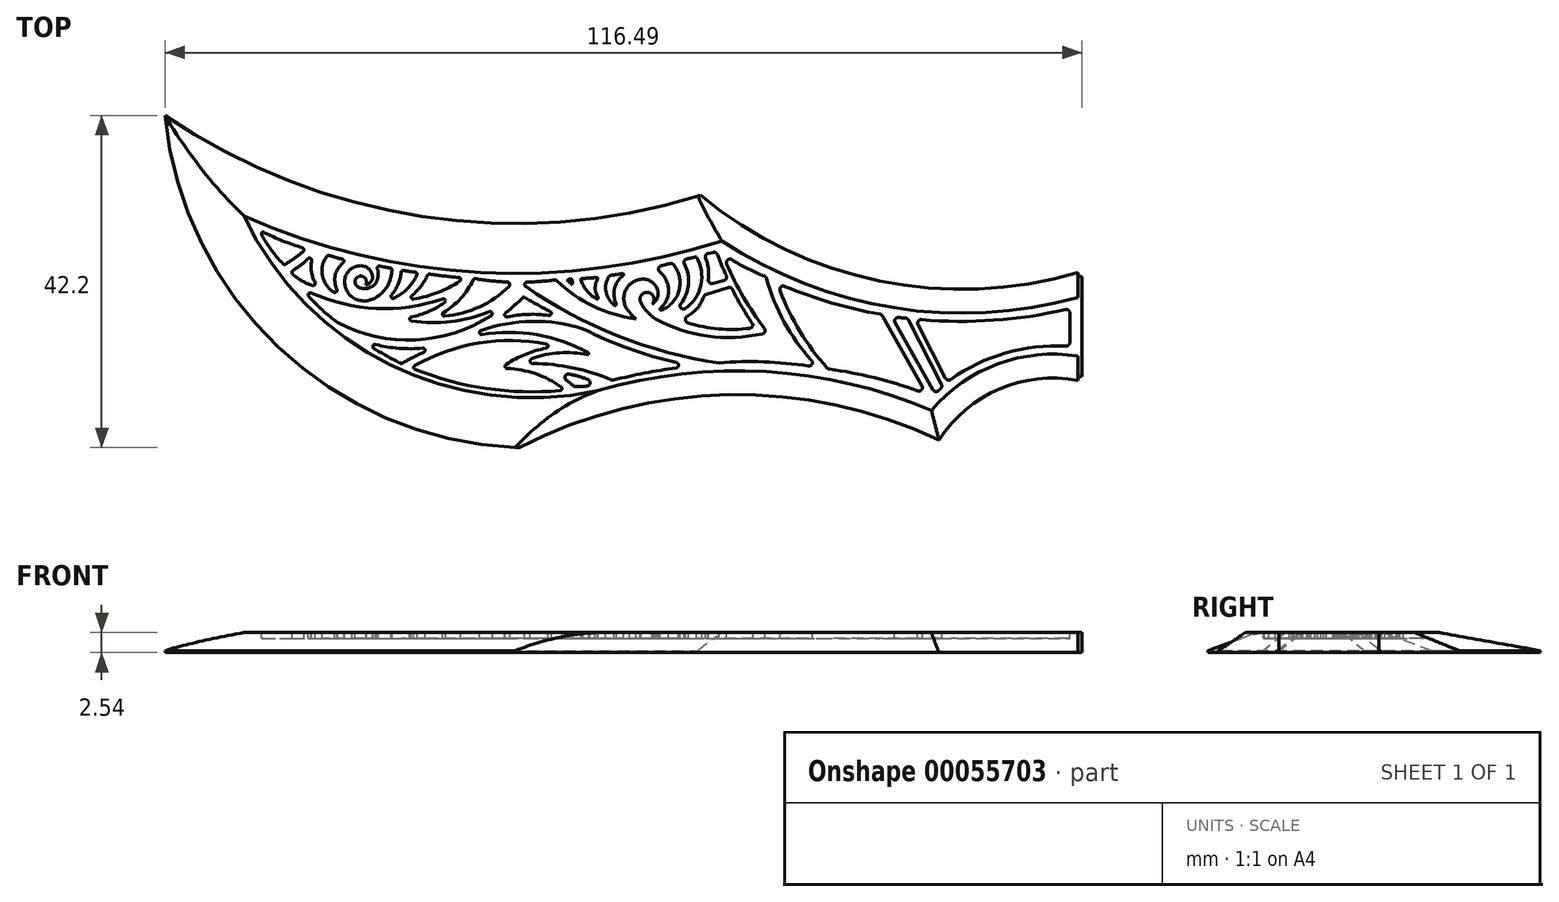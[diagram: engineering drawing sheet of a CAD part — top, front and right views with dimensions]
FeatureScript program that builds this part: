
annotation { "Feature Type Name" : "Feature", "Feature Type Description" : "" }
export const myFeature = defineFeature(function(context is Context, id is Id, definition is map)
    precondition{}
    {
        {
            var Q0;
            Q0=qCreatedBy(makeId("Top.planeOp"),FACE);
            var sketch = newSketch(context, id + "F0", { "sketchPlane" : qUnion([Q0])});
            skLineSegment(sketch, "E0", {"start": v(52.01, 15.28) * mm, "end": v(52.01, 0) * mm});
            skArc(sketch, "E1", {"start": v(4.94, 24.58) * mm, "mid": v(27.32, 14.1) * mm, "end": v(52.01, 15.28) * mm});
            skArc(sketch, "E2", {"start": v(-63.97, 34.45) * mm, "mid": v(-30.66, 21.52) * mm, "end": v(4.94, 24.58) * mm});
            skArc(sketch, "E3", {"start": v(-63.97, 34.45) * mm, "mid": v(-48.77, 4.29) * mm, "end": v(-17.2, -7.77) * mm});
            skArc(sketch, "E4", {"start": v(34.67, -7.77) * mm, "mid": v(8.73, -1.81) * mm, "end": v(-17.2, -7.77) * mm});
            skArc(sketch, "E5", {"start": v(52.01, 0) * mm, "mid": v(42.1, -1.13) * mm, "end": v(34.67, -7.77) * mm});
            skLineSegment(sketch, "E6.bottom", {"start": v(52.01, 15.28) * mm, "end": v(52.52, 15.28) * mm});
            skLineSegment(sketch, "E6.top", {"start": v(52.01, 0) * mm, "end": v(52.52, 0) * mm});
            skLineSegment(sketch, "E6.right", {"start": v(52.52, 15.28) * mm, "end": v(52.52, 0) * mm});
            skLineSegment(sketch, "E7", {"start": v(52.01, 13.97) * mm, "end": v(52.52, 13.97) * mm});
            skLineSegment(sketch, "E8", {"start": v(52.01, 1.27) * mm, "end": v(52.52, 1.27) * mm});
            skSolve(sketch);
        }
        {
            var Q0;
            {var subQ4=sQuery(id+"F0.wireOp",EDGE,"E1");Q0=makeQuery(id+"F0.imprint","IMPRINT",FACE,{"disambiguationData":[TD([[makeQuery(id+"F0.imprint","IMPRINT",EDGE,{"derivedFrom":subQ4}),-1.0]])]});}
            extrude(context, id + "F1", {"entities" : qUnion([Q0]), "depth" : 2.54 * mm});
        }
        {
            var Q0;
            Q0=makeQuery(id+"F1.opExtrude","CAP_EDGE",EDGE,{"disambiguationData":[OSD([sQuery(id+"F0.wireOp",EDGE,"E5")])],"isStart":false});
            var Q1;
            Q1=makeQuery(id+"F1.opExtrude","CAP_EDGE",EDGE,{"disambiguationData":[OSD([sQuery(id+"F0.wireOp",EDGE,"E1")])],"isStart":false});
            var Q2;
            Q2=makeQuery(id+"F1.opExtrude","CAP_EDGE",EDGE,{"disambiguationData":[OSD([sQuery(id+"F0.wireOp",EDGE,"E4")])],"isStart":false});
            chamfer(context, id + "F2", {"entities" : qUnion([Q0, Q1, Q2]), "chamferType" : ChamferType.OFFSET_ANGLE, "width" : 3.8 * mm, "oppositeDirection" : true, "angle" : 40 * degree, "tangentPropagation" : true});
        }
        {
            var Q0;
            Q0=makeQuery(id+"F1.opExtrude","CAP_EDGE",EDGE,{"disambiguationData":[OSD([sQuery(id+"F0.wireOp",EDGE,"E2")])],"isStart":false});
            var Q1;
            Q1=makeQuery(id+"F1.opExtrude","CAP_EDGE",EDGE,{"disambiguationData":[OSD([sQuery(id+"F0.wireOp",EDGE,"E3")])],"isStart":false});
            chamfer(context, id + "F3", {"entities" : qUnion([Q0, Q1]), "chamferType" : ChamferType.OFFSET_ANGLE, "width" : 6.35 * mm, "oppositeDirection" : true, "angle" : 20 * degree, "tangentPropagation" : true});
        }
        {
            var Q0;
            Q0=makeQuery(id+"F1.opExtrude","CAP_FACE",FACE,{"disambiguationData":[OSD([sQuery(id+"F0.wireOp",EDGE,"E1"),sQuery(id+"F0.wireOp",EDGE,"E2"),sQuery(id+"F0.wireOp",EDGE,"E3"),sQuery(id+"F0.wireOp",EDGE,"E4"),sQuery(id+"F0.wireOp",EDGE,"E5"),sQuery(id+"F0.wireOp",EDGE,"E0")])],"isStart":false});
            var sketch = newSketch(context, id + "F4", { "sketchPlane" : qUnion([Q0])});
            skPoint(sketch, "E9", {"position": v(-53.92, 21.64) * mm});
            skPoint(sketch, "E10", {"position": v(6.79, 18.5) * mm});
            skPoint(sketch, "E11", {"position": v(52.01, 11.32) * mm});
            skPoint(sketch, "E12", {"position": v(52.01, 3.87) * mm});
            skPoint(sketch, "E13", {"position": v(33.4, -3.01) * mm});
            skPoint(sketch, "E14", {"position": v(-8.98, -0.53) * mm});
            skArc(sketch, "E15", {"start": v(-53.92, 21.64) * mm, "mid": v(-23.86, 14.49) * mm, "end": v(6.79, 18.5) * mm});
            skArc(sketch, "E16", {"start": v(6.79, 18.5) * mm, "mid": v(28.62, 10) * mm, "end": v(52.01, 11.32) * mm});
            skArc(sketch, "E17", {"start": v(-53.92, 21.64) * mm, "mid": v(-35.3, 2.75) * mm, "end": v(-8.98, -0.53) * mm});
            skArc(sketch, "E18", {"start": v(33.4, -3.01) * mm, "mid": v(12.43, 1.9) * mm, "end": v(-8.98, -0.53) * mm});
            skArc(sketch, "E19", {"start": v(52.01, 3.87) * mm, "mid": v(41.8, 2.86) * mm, "end": v(33.4, -3.01) * mm});
            skLineSegment(sketch, "E20", {"start": v(52.01, 11.32) * mm, "end": v(52.01, 3.87) * mm});
            skArc(sketch, "E21", {"start": v(-51.68, 19.31) * mm, "mid": v(-50.46, 17.36) * mm, "end": v(-48.97, 15.6) * mm});
            skArc(sketch, "E22", {"start": v(-51.41, 19.59) * mm, "mid": v(-49, 18.5) * mm, "end": v(-46.5, 17.62) * mm});
            skArc(sketch, "E23", {"start": v(-48.65, 15.55) * mm, "mid": v(-47.5, 16.31) * mm, "end": v(-46.4, 17.16) * mm});
            skPoint(sketch, "E24.visualSharp", {"position": v(-51.95, 19.85) * mm});
            skArc(sketch, "E24.filletArc", {"start": v(-51.41, 19.59) * mm, "mid": v(-51.64, 19.55) * mm, "end": v(-51.68, 19.31) * mm});
            skArc(sketch, "E25", {"start": v(14.75, 12.73) * mm, "mid": v(20.7, 10.64) * mm, "end": v(26.86, 9.2) * mm});
            skArc(sketch, "E26", {"start": v(14.17, 12.17) * mm, "mid": v(16.71, 7) * mm, "end": v(20.16, 2.37) * mm});
            skArc(sketch, "E27", {"start": v(31.66, -0.55) * mm, "mid": v(26.11, 1.13) * mm, "end": v(20.42, 2.23) * mm});
            skArc(sketch, "E28", {"start": v(34.6, -0.23) * mm, "mid": v(34.45, -0.36) * mm, "end": v(34.32, -0.5) * mm});
            skArc(sketch, "E29", {"start": v(8.04, 16.13) * mm, "mid": v(10.07, 14.98) * mm, "end": v(12.2, 14.02) * mm});
            skArc(sketch, "E30", {"start": v(7.4, 15.58) * mm, "mid": v(9.53, 11.34) * mm, "end": v(12.19, 7.4) * mm});
            skArc(sketch, "E31", {"start": v(12.46, 13.73) * mm, "mid": v(14.7, 8.2) * mm, "end": v(18.16, 3.33) * mm});
            skArc(sketch, "E32", {"start": v(-1.66, 8.6) * mm, "mid": v(4.96, 6.42) * mm, "end": v(11.93, 6.7) * mm});
            skArc(sketch, "E33", {"start": v(-2.1, 10.46) * mm, "mid": v(-2.1, 11.7) * mm, "end": v(-3.35, 11.72) * mm});
            skArc(sketch, "E34", {"start": v(-3.35, 11.72) * mm, "mid": v(-3.6, 11.22) * mm, "end": v(-3.5, 10.66) * mm});
            skArc(sketch, "E35", {"start": v(-3.5, 10.66) * mm, "mid": v(-2.73, 9.5) * mm, "end": v(-1.66, 8.6) * mm});
            skArc(sketch, "E36", {"start": v(-2.1, 10.46) * mm, "mid": v(-1.43, 11.25) * mm, "end": v(-1.38, 12.29) * mm});
            skArc(sketch, "E37", {"start": v(-1.38, 12.29) * mm, "mid": v(-2.25, 13.36) * mm, "end": v(-3.6, 13.6) * mm});
            skArc(sketch, "E38", {"start": v(-3.6, 13.6) * mm, "mid": v(-5.56, 11.94) * mm, "end": v(-4.95, 9.45) * mm});
            skArc(sketch, "E39", {"start": v(-17.93, 13.29) * mm, "mid": v(-16.2, 13.36) * mm, "end": v(-14.47, 13.54) * mm});
            skArc(sketch, "E40", {"start": v(-18.12, 12.68) * mm, "mid": v(-6.4, 6.42) * mm, "end": v(6.42, 3.01) * mm});
            skArc(sketch, "E41", {"start": v(17.77, 2.6) * mm, "mid": v(12.1, 3.14) * mm, "end": v(6.42, 3.01) * mm});
            skArc(sketch, "E42", {"start": v(-4.95, 9.45) * mm, "mid": v(-4.58, 9) * mm, "end": v(-4.15, 8.6) * mm});
            skArc(sketch, "E43", {"start": v(-14.19, 13.45) * mm, "mid": v(-9.56, 10.2) * mm, "end": v(-4.15, 8.6) * mm});
            skArc(sketch, "E44", {"start": v(-10.83, 7.33) * mm, "mid": v(-5.03, 4.82) * mm, "end": v(1.02, 3.03) * mm});
            skArc(sketch, "E45", {"start": v(-10.83, 7.33) * mm, "mid": v(-17.34, 8.28) * mm, "end": v(-23.83, 7.13) * mm});
            skArc(sketch, "E46", {"start": v(-10.21, 4.3) * mm, "mid": v(-16.76, 6.59) * mm, "end": v(-23.7, 6.62) * mm});
            skArc(sketch, "E47", {"start": v(-10.3, 4.04) * mm, "mid": v(-13.86, 4.28) * mm, "end": v(-17.34, 3.56) * mm});
            skArc(sketch, "E48", {"start": v(-7.22, 0.83) * mm, "mid": v(-12.12, 2.38) * mm, "end": v(-17.23, 2.91) * mm});
            skArc(sketch, "E49", {"start": v(1, 2.37) * mm, "mid": v(-3.03, 1.7) * mm, "end": v(-7, 0.82) * mm});
            skArc(sketch, "E50", {"start": v(-42.02, 8.13) * mm, "mid": v(-32.13, 5.91) * mm, "end": v(-22.5, 9.04) * mm});
            skArc(sketch, "E51", {"start": v(-32.63, 8.34) * mm, "mid": v(-27.6, 8.25) * mm, "end": v(-22.74, 9.5) * mm});
            skArc(sketch, "E52", {"start": v(-32.64, 8.86) * mm, "mid": v(-30.45, 9.53) * mm, "end": v(-28.45, 10.65) * mm});
            skArc(sketch, "E53", {"start": v(-45.4, 11.89) * mm, "mid": v(-37.12, 9.93) * mm, "end": v(-28.7, 11.12) * mm});
            skArc(sketch, "E54", {"start": v(-45.7, 11.47) * mm, "mid": v(-43.95, 9.7) * mm, "end": v(-42.02, 8.13) * mm});
            skArc(sketch, "E55", {"start": v(-1.03, 9.95) * mm, "mid": v(0.02, 12.27) * mm, "end": v(-1.1, 14.56) * mm});
            skPoint(sketch, "E55.startSnap0", {"position": v(-30.5, 9.5) * mm});
            skArc(sketch, "E56", {"start": v(-0.93, 15.34) * mm, "mid": v(-0.37, 15.48) * mm, "end": v(0.18, 15.63) * mm});
            skArc(sketch, "E57", {"start": v(-0.9, 9.72) * mm, "mid": v(1.35, 12.2) * mm, "end": v(0.65, 15.48) * mm});
            skArc(sketch, "E58", {"start": v(1.57, 10.55) * mm, "mid": v(2.54, 12.99) * mm, "end": v(2.01, 15.56) * mm});
            skArc(sketch, "E59", {"start": v(2.17, 9.92) * mm, "mid": v(4.14, 12.93) * mm, "end": v(3.53, 16.48) * mm});
            skArc(sketch, "E60", {"start": v(2.3, 16.2) * mm, "mid": v(2.92, 16.34) * mm, "end": v(3.53, 16.48) * mm});
            skArc(sketch, "E61", {"start": v(-7.41, 14.12) * mm, "mid": v(-6.63, 14.23) * mm, "end": v(-5.84, 14.35) * mm});
            skArc(sketch, "E62", {"start": v(-5.74, 14.1) * mm, "mid": v(-6.84, 12.46) * mm, "end": v(-6.64, 10.49) * mm});
            skArc(sketch, "E63", {"start": v(-7.5, 14.06) * mm, "mid": v(-7.94, 12.05) * mm, "end": v(-6.85, 10.32) * mm});
            skArc(sketch, "E64", {"start": v(-11, 13.73) * mm, "mid": v(-10.07, 13.78) * mm, "end": v(-9.13, 13.85) * mm});
            skArc(sketch, "E65", {"start": v(-9, 13.65) * mm, "mid": v(-9.3, 12.47) * mm, "end": v(-8.94, 11.32) * mm});
            skArc(sketch, "E66", {"start": v(-11.13, 13.55) * mm, "mid": v(-10.35, 12.16) * mm, "end": v(-9.12, 11.13) * mm});
            skArc(sketch, "E67", {"start": v(-12.67, 13.62) * mm, "mid": v(-12.53, 13.63) * mm, "end": v(-12.4, 13.65) * mm});
            skArc(sketch, "E68", {"start": v(-12.75, 13.39) * mm, "mid": v(-12.57, 13.22) * mm, "end": v(-12.37, 13.07) * mm});
            skArc(sketch, "E69", {"start": v(-12.25, 13.54) * mm, "mid": v(-12.21, 13.38) * mm, "end": v(-12.16, 13.22) * mm});
            skArc(sketch, "E70", {"start": v(-15.52, 5.4) * mm, "mid": v(-24.12, 5.52) * mm, "end": v(-32.22, 2.66) * mm});
            skArc(sketch, "E71", {"start": v(-15.52, 4.88) * mm, "mid": v(-18.18, 4.1) * mm, "end": v(-20.63, 2.8) * mm});
            skArc(sketch, "E72", {"start": v(-13.64, -0.03) * mm, "mid": v(-16.9, 1.63) * mm, "end": v(-20.5, 2.3) * mm});
            skArc(sketch, "E73", {"start": v(-32.19, 2.18) * mm, "mid": v(-23.14, -0.25) * mm, "end": v(-13.77, -0.52) * mm});
            skArc(sketch, "E74", {"start": v(-31.07, 4.36) * mm, "mid": v(-32.45, 3.7) * mm, "end": v(-33.8, 2.98) * mm});
            skArc(sketch, "E75", {"start": v(-37.22, 5.34) * mm, "mid": v(-34.23, 4.85) * mm, "end": v(-31.2, 4.87) * mm});
            skArc(sketch, "E76", {"start": v(-37.43, 4.86) * mm, "mid": v(-35.76, 3.87) * mm, "end": v(-34.04, 2.97) * mm});
            skArc(sketch, "E77", {"start": v(-37.6, 13.75) * mm, "mid": v(-37.93, 14.8) * mm, "end": v(-38.9, 15.33) * mm});
            skArc(sketch, "E78", {"start": v(-38.9, 15.33) * mm, "mid": v(-40.32, 14.96) * mm, "end": v(-41.1, 13.72) * mm});
            skArc(sketch, "E79", {"start": v(-41.1, 13.72) * mm, "mid": v(-40.97, 12.42) * mm, "end": v(-40.18, 11.37) * mm});
            skArc(sketch, "E80", {"start": v(-40.18, 11.37) * mm, "mid": v(-38.57, 10.88) * mm, "end": v(-36.98, 11.43) * mm});
            skArc(sketch, "E81", {"start": v(-38.43, 13.62) * mm, "mid": v(-39.58, 13.84) * mm, "end": v(-39.45, 12.67) * mm});
            skArc(sketch, "E82", {"start": v(-38.43, 12.89) * mm, "mid": v(-38.37, 13.25) * mm, "end": v(-38.43, 13.62) * mm});
            skArc(sketch, "E83", {"start": v(-38.43, 12.89) * mm, "mid": v(-37.9, 13.2) * mm, "end": v(-37.6, 13.75) * mm});
            skArc(sketch, "E84", {"start": v(-39.45, 12.67) * mm, "mid": v(-38.25, 12.47) * mm, "end": v(-37.2, 13.1) * mm});
            skArc(sketch, "E85", {"start": v(-37.2, 13.1) * mm, "mid": v(-36.88, 14) * mm, "end": v(-36.98, 14.96) * mm});
            skArc(sketch, "E86", {"start": v(-36.98, 11.43) * mm, "mid": v(-35.64, 12.88) * mm, "end": v(-35.12, 14.8) * mm});
            skArc(sketch, "E87", {"start": v(-36.67, 15.3) * mm, "mid": v(-36.01, 15.17) * mm, "end": v(-35.35, 15.06) * mm});
            skArc(sketch, "E88", {"start": v(-35.18, 11.64) * mm, "mid": v(-34.35, 12.99) * mm, "end": v(-33.96, 14.53) * mm});
            skArc(sketch, "E89", {"start": v(-34.86, 11.23) * mm, "mid": v(-33.16, 12.44) * mm, "end": v(-31.97, 14.17) * mm});
            skArc(sketch, "E90", {"start": v(-33.64, 14.76) * mm, "mid": v(-32.92, 14.62) * mm, "end": v(-32.19, 14.54) * mm});
            skArc(sketch, "E91", {"start": v(-41.33, 15.72) * mm, "mid": v(-42.32, 14.17) * mm, "end": v(-42.13, 12.34) * mm});
            skArc(sketch, "E92", {"start": v(-43.4, 16.55) * mm, "mid": v(-43.97, 14.08) * mm, "end": v(-42.5, 12) * mm});
            skArc(sketch, "E93", {"start": v(-43.1, 16.65) * mm, "mid": v(-42.27, 16.4) * mm, "end": v(-41.43, 16.19) * mm});
            skArc(sketch, "E94", {"start": v(-47.72, 14.7) * mm, "mid": v(-46.71, 15.43) * mm, "end": v(-45.77, 16.24) * mm});
            skArc(sketch, "E95", {"start": v(-45.33, 16) * mm, "mid": v(-45.35, 14.57) * mm, "end": v(-44.9, 13.21) * mm});
            skArc(sketch, "E96", {"start": v(-47.75, 14.28) * mm, "mid": v(-46.55, 13.43) * mm, "end": v(-45.22, 12.84) * mm});
            skArc(sketch, "E97", {"start": v(-32.58, 11.57) * mm, "mid": v(-31.45, 12.75) * mm, "end": v(-30.6, 14.14) * mm});
            skArc(sketch, "E98", {"start": v(-32.36, 11.1) * mm, "mid": v(-29.32, 11.94) * mm, "end": v(-26.5, 13.38) * mm});
            skArc(sketch, "E99", {"start": v(-30.31, 14.28) * mm, "mid": v(-28.48, 14.03) * mm, "end": v(-26.63, 13.86) * mm});
            skArc(sketch, "E100", {"start": v(-28.58, 9.43) * mm, "mid": v(-26.38, 11.2) * mm, "end": v(-24.82, 13.55) * mm});
            skArc(sketch, "E101", {"start": v(-28.43, 8.93) * mm, "mid": v(-24.01, 10.12) * mm, "end": v(-20.25, 12.7) * mm});
            skArc(sketch, "E102", {"start": v(-24.53, 13.7) * mm, "mid": v(-22.51, 13.42) * mm, "end": v(-20.48, 13.28) * mm});
            skArc(sketch, "E103", {"start": v(-20.7, 9.33) * mm, "mid": v(-19.6, 10.27) * mm, "end": v(-18.55, 11.26) * mm});
            skArc(sketch, "E104", {"start": v(-18.23, 11.3) * mm, "mid": v(-16.64, 10.4) * mm, "end": v(-15.03, 9.54) * mm});
            skArc(sketch, "E105", {"start": v(-15.18, 9.04) * mm, "mid": v(-17.84, 9.17) * mm, "end": v(-20.5, 8.86) * mm});
            skArc(sketch, "E106", {"start": v(2.37, 8.9) * mm, "mid": v(3.66, 9.97) * mm, "end": v(4.5, 11.42) * mm});
            skArc(sketch, "E107", {"start": v(2.46, 8.1) * mm, "mid": v(6.35, 7.33) * mm, "end": v(10.33, 7.4) * mm});
            skArc(sketch, "E108", {"start": v(8.13, 12.34) * mm, "mid": v(9.29, 10.16) * mm, "end": v(10.63, 8.1) * mm});
            skArc(sketch, "E109", {"start": v(5.06, 13.6) * mm, "mid": v(5.07, 14.99) * mm, "end": v(4.72, 16.32) * mm});
            skArc(sketch, "E110", {"start": v(5.04, 16.92) * mm, "mid": v(5.37, 16.99) * mm, "end": v(5.7, 17.06) * mm});
            skArc(sketch, "E111", {"start": v(6.2, 16.78) * mm, "mid": v(6.75, 15.44) * mm, "end": v(7.36, 14.12) * mm});
            skLineSegment(sketch, "E112", {"start": v(5.6, 13.11) * mm, "end": v(7.07, 13.5) * mm});
            skLineSegment(sketch, "E113", {"start": v(4.78, 11.7) * mm, "end": v(7.6, 12.57) * mm});
            skLineSegment(sketch, "E114", {"start": v(27.17, 8.98) * mm, "end": v(32.2, 0.09) * mm});
            skLineSegment(sketch, "E115", {"start": v(28.79, 8.12) * mm, "end": v(33.62, -0.41) * mm});
            skLineSegment(sketch, "E116", {"start": v(34.67, 0.29) * mm, "end": v(30.47, 8.46) * mm});
            skLineSegment(sketch, "E117", {"start": v(31.7, 7.86) * mm, "end": v(35.21, 1.05) * mm});
            skPoint(sketch, "E118.visualSharp", {"position": v(-46.04, 17.48) * mm});
            skArc(sketch, "E118.filletArc", {"start": v(-46.4, 17.16) * mm, "mid": v(-46.31, 17.42) * mm, "end": v(-46.5, 17.62) * mm});
            skPoint(sketch, "E119.visualSharp", {"position": v(-48.83, 15.45) * mm});
            skArc(sketch, "E119.filletArc", {"start": v(-48.97, 15.6) * mm, "mid": v(-48.82, 15.52) * mm, "end": v(-48.65, 15.55) * mm});
            skPoint(sketch, "E120.visualSharp", {"position": v(-48.01, 14.52) * mm});
            skArc(sketch, "E120.filletArc", {"start": v(-47.72, 14.7) * mm, "mid": v(-47.84, 14.5) * mm, "end": v(-47.75, 14.28) * mm});
            skPoint(sketch, "E121.visualSharp", {"position": v(-44.54, 12.65) * mm});
            skArc(sketch, "E121.filletArc", {"start": v(-45.22, 12.84) * mm, "mid": v(-44.93, 12.92) * mm, "end": v(-44.9, 13.21) * mm});
            skPoint(sketch, "E122.visualSharp", {"position": v(-44.98, 17.08) * mm});
            skArc(sketch, "E122.filletArc", {"start": v(-45.33, 16) * mm, "mid": v(-45.47, 16.28) * mm, "end": v(-45.77, 16.24) * mm});
            skPoint(sketch, "E123.visualSharp", {"position": v(-43.27, 16.7) * mm});
            skArc(sketch, "E123.filletArc", {"start": v(-43.1, 16.65) * mm, "mid": v(-43.26, 16.65) * mm, "end": v(-43.4, 16.55) * mm});
            skPoint(sketch, "E124.visualSharp", {"position": v(-40.79, 16.05) * mm});
            skArc(sketch, "E124.filletArc", {"start": v(-41.33, 15.72) * mm, "mid": v(-41.23, 15.99) * mm, "end": v(-41.43, 16.19) * mm});
            skPoint(sketch, "E125.visualSharp", {"position": v(-41.67, 11.66) * mm});
            skArc(sketch, "E125.filletArc", {"start": v(-42.5, 12) * mm, "mid": v(-42.19, 12.03) * mm, "end": v(-42.13, 12.34) * mm});
            skPoint(sketch, "E126.visualSharp", {"position": v(-46.5, 12.41) * mm});
            skArc(sketch, "E126.filletArc", {"start": v(-45.4, 11.89) * mm, "mid": v(-45.71, 11.8) * mm, "end": v(-45.7, 11.47) * mm});
            skPoint(sketch, "E127.visualSharp", {"position": v(-27.25, 11.66) * mm});
            skArc(sketch, "E127.filletArc", {"start": v(-28.45, 10.65) * mm, "mid": v(-28.37, 10.99) * mm, "end": v(-28.7, 11.12) * mm});
            skPoint(sketch, "E128.visualSharp", {"position": v(-33.38, 10.97) * mm});
            skArc(sketch, "E128.filletArc", {"start": v(-32.58, 11.57) * mm, "mid": v(-32.65, 11.26) * mm, "end": v(-32.36, 11.1) * mm});
            skPoint(sketch, "E129.visualSharp", {"position": v(-36.05, 10.8) * mm});
            skArc(sketch, "E129.filletArc", {"start": v(-35.18, 11.64) * mm, "mid": v(-35.19, 11.3) * mm, "end": v(-34.86, 11.23) * mm});
            skPoint(sketch, "E130.visualSharp", {"position": v(-31.82, 14.52) * mm});
            skArc(sketch, "E130.filletArc", {"start": v(-31.97, 14.17) * mm, "mid": v(-31.98, 14.41) * mm, "end": v(-32.19, 14.54) * mm});
            skPoint(sketch, "E131.visualSharp", {"position": v(-33.93, 14.83) * mm});
            skArc(sketch, "E131.filletArc", {"start": v(-33.64, 14.76) * mm, "mid": v(-33.85, 14.71) * mm, "end": v(-33.96, 14.53) * mm});
            skPoint(sketch, "E132.visualSharp", {"position": v(-37.2, 15.44) * mm});
            skArc(sketch, "E132.filletArc", {"start": v(-36.67, 15.3) * mm, "mid": v(-36.92, 15.22) * mm, "end": v(-36.98, 14.96) * mm});
            skPoint(sketch, "E133.visualSharp", {"position": v(-35.13, 15.03) * mm});
            skArc(sketch, "E133.filletArc", {"start": v(-35.12, 14.8) * mm, "mid": v(-35.19, 14.97) * mm, "end": v(-35.35, 15.06) * mm});
            skPoint(sketch, "E134.visualSharp", {"position": v(-20.29, 10.72) * mm});
            skArc(sketch, "E134.filletArc", {"start": v(-22.5, 9.04) * mm, "mid": v(-22.4, 9.38) * mm, "end": v(-22.74, 9.5) * mm});
            skPoint(sketch, "E135.visualSharp", {"position": v(-29.7, 8.88) * mm});
            skArc(sketch, "E135.filletArc", {"start": v(-28.58, 9.43) * mm, "mid": v(-28.7, 9.12) * mm, "end": v(-28.43, 8.93) * mm});
            skPoint(sketch, "E136.visualSharp", {"position": v(-25.86, 13.82) * mm});
            skArc(sketch, "E136.filletArc", {"start": v(-26.5, 13.38) * mm, "mid": v(-26.4, 13.67) * mm, "end": v(-26.63, 13.86) * mm});
            skPoint(sketch, "E137.visualSharp", {"position": v(-30.5, 14.31) * mm});
            skArc(sketch, "E137.filletArc", {"start": v(-30.31, 14.28) * mm, "mid": v(-30.48, 14.26) * mm, "end": v(-30.6, 14.14) * mm});
            skPoint(sketch, "E138.visualSharp", {"position": v(-24.73, 13.74) * mm});
            skArc(sketch, "E138.filletArc", {"start": v(-24.53, 13.7) * mm, "mid": v(-24.7, 13.68) * mm, "end": v(-24.82, 13.55) * mm});
            skPoint(sketch, "E139.visualSharp", {"position": v(-38.9, 5.85) * mm});
            skArc(sketch, "E139.filletArc", {"start": v(-37.22, 5.34) * mm, "mid": v(-37.53, 5.2) * mm, "end": v(-37.43, 4.86) * mm});
            skPoint(sketch, "E140.visualSharp", {"position": v(-28.92, 5.22) * mm});
            skArc(sketch, "E140.filletArc", {"start": v(-31.07, 4.36) * mm, "mid": v(-30.92, 4.67) * mm, "end": v(-31.2, 4.87) * mm});
            skPoint(sketch, "E141.visualSharp", {"position": v(-34.33, 8.68) * mm});
            skArc(sketch, "E141.filletArc", {"start": v(-32.64, 8.86) * mm, "mid": v(-32.86, 8.6) * mm, "end": v(-32.63, 8.34) * mm});
            skPoint(sketch, "E142.visualSharp", {"position": v(-32.69, 2.38) * mm});
            skArc(sketch, "E142.filletArc", {"start": v(-32.22, 2.66) * mm, "mid": v(-32.35, 2.4) * mm, "end": v(-32.19, 2.18) * mm});
            skPoint(sketch, "E143.visualSharp", {"position": v(-33.91, 2.9) * mm});
            skArc(sketch, "E143.filletArc", {"start": v(-34.04, 2.97) * mm, "mid": v(-33.91, 2.94) * mm, "end": v(-33.8, 2.98) * mm});
            skPoint(sketch, "E144.visualSharp", {"position": v(-21.3, 2.32) * mm});
            skArc(sketch, "E144.filletArc", {"start": v(-20.63, 2.8) * mm, "mid": v(-20.74, 2.5) * mm, "end": v(-20.5, 2.3) * mm});
            skPoint(sketch, "E145.visualSharp", {"position": v(-14.06, 5.07) * mm});
            skArc(sketch, "E145.filletArc", {"start": v(-15.52, 4.88) * mm, "mid": v(-15.3, 5.14) * mm, "end": v(-15.52, 5.4) * mm});
            skPoint(sketch, "E146.visualSharp", {"position": v(-13.09, -0.45) * mm});
            skArc(sketch, "E146.filletArc", {"start": v(-13.77, -0.52) * mm, "mid": v(-13.54, -0.32) * mm, "end": v(-13.64, -0.03) * mm});
            skPoint(sketch, "E147.visualSharp", {"position": v(-26.59, 5.94) * mm});
            skArc(sketch, "E147.filletArc", {"start": v(-23.83, 7.13) * mm, "mid": v(-24, 6.82) * mm, "end": v(-23.7, 6.62) * mm});
            skPoint(sketch, "E148.visualSharp", {"position": v(-18.4, 11.41) * mm});
            skArc(sketch, "E148.filletArc", {"start": v(-18.23, 11.3) * mm, "mid": v(-18.4, 11.34) * mm, "end": v(-18.55, 11.26) * mm});
            skPoint(sketch, "E149.visualSharp", {"position": v(-13.16, 8.64) * mm});
            skArc(sketch, "E149.filletArc", {"start": v(-15.18, 9.04) * mm, "mid": v(-14.9, 9.23) * mm, "end": v(-15.03, 9.54) * mm});
            skPoint(sketch, "E150.visualSharp", {"position": v(-21.73, 8.56) * mm});
            skArc(sketch, "E150.filletArc", {"start": v(-20.7, 9.33) * mm, "mid": v(-20.78, 9.01) * mm, "end": v(-20.5, 8.86) * mm});
            skPoint(sketch, "E151.visualSharp", {"position": v(-19.72, 13.27) * mm});
            skArc(sketch, "E151.filletArc", {"start": v(-20.25, 12.7) * mm, "mid": v(-20.18, 13.07) * mm, "end": v(-20.48, 13.28) * mm});
            skPoint(sketch, "E152.visualSharp", {"position": v(-18.97, 2.86) * mm});
            skArc(sketch, "E152.filletArc", {"start": v(-17.34, 3.56) * mm, "mid": v(-17.56, 3.2) * mm, "end": v(-17.23, 2.91) * mm});
            skPoint(sketch, "E153.visualSharp", {"position": v(-7.12, 0.79) * mm});
            skArc(sketch, "E153.filletArc", {"start": v(-7.22, 0.83) * mm, "mid": v(-7.11, 0.8) * mm, "end": v(-7, 0.82) * mm});
            skPoint(sketch, "E154.visualSharp", {"position": v(2.97, 2.62) * mm});
            skArc(sketch, "E154.filletArc", {"start": v(1, 2.37) * mm, "mid": v(1.28, 2.7) * mm, "end": v(1.02, 3.03) * mm});
            skPoint(sketch, "E155.visualSharp", {"position": v(-19, 13.3) * mm});
            skArc(sketch, "E155.filletArc", {"start": v(-17.93, 13.29) * mm, "mid": v(-18.25, 13.05) * mm, "end": v(-18.12, 12.68) * mm});
            skPoint(sketch, "E156.visualSharp", {"position": v(-14.3, 13.57) * mm});
            skArc(sketch, "E156.filletArc", {"start": v(-14.19, 13.45) * mm, "mid": v(-14.32, 13.53) * mm, "end": v(-14.47, 13.54) * mm});
            skPoint(sketch, "E157.visualSharp", {"position": v(-12.98, 13.62) * mm});
            skArc(sketch, "E157.filletArc", {"start": v(-12.67, 13.62) * mm, "mid": v(-12.79, 13.53) * mm, "end": v(-12.75, 13.39) * mm});
            skPoint(sketch, "E158.visualSharp", {"position": v(-12.26, 13.67) * mm});
            skArc(sketch, "E158.filletArc", {"start": v(-12.25, 13.54) * mm, "mid": v(-12.3, 13.62) * mm, "end": v(-12.4, 13.65) * mm});
            skPoint(sketch, "E159.visualSharp", {"position": v(-11.95, 12.8) * mm});
            skArc(sketch, "E159.filletArc", {"start": v(-12.37, 13.07) * mm, "mid": v(-12.21, 13.07) * mm, "end": v(-12.16, 13.22) * mm});
            skPoint(sketch, "E160.visualSharp", {"position": v(-11.18, 13.72) * mm});
            skArc(sketch, "E160.filletArc", {"start": v(-11, 13.73) * mm, "mid": v(-11.11, 13.67) * mm, "end": v(-11.13, 13.55) * mm});
            skPoint(sketch, "E161.visualSharp", {"position": v(-8.84, 13.88) * mm});
            skArc(sketch, "E161.filletArc", {"start": v(-9, 13.65) * mm, "mid": v(-9, 13.79) * mm, "end": v(-9.13, 13.85) * mm});
            skPoint(sketch, "E162.visualSharp", {"position": v(-8.5, 10.83) * mm});
            skArc(sketch, "E162.filletArc", {"start": v(-9.12, 11.13) * mm, "mid": v(-8.96, 11.15) * mm, "end": v(-8.94, 11.32) * mm});
            skPoint(sketch, "E163.visualSharp", {"position": v(-6.4, 10.06) * mm});
            skArc(sketch, "E163.filletArc", {"start": v(-6.85, 10.32) * mm, "mid": v(-6.68, 10.33) * mm, "end": v(-6.64, 10.49) * mm});
            skPoint(sketch, "E164.visualSharp", {"position": v(-5.02, 14.5) * mm});
            skArc(sketch, "E164.filletArc", {"start": v(-5.74, 14.1) * mm, "mid": v(-5.7, 14.27) * mm, "end": v(-5.84, 14.35) * mm});
            skPoint(sketch, "E165.visualSharp", {"position": v(-7.47, 14.11) * mm});
            skArc(sketch, "E165.filletArc", {"start": v(-7.41, 14.12) * mm, "mid": v(-7.47, 14.1) * mm, "end": v(-7.5, 14.06) * mm});
            skPoint(sketch, "E166.visualSharp", {"position": v(-9.4, 3.82) * mm});
            skArc(sketch, "E166.filletArc", {"start": v(-10.3, 4.04) * mm, "mid": v(-10.15, 4.13) * mm, "end": v(-10.21, 4.3) * mm});
            skPoint(sketch, "E167.visualSharp", {"position": v(-1.73, 9.5) * mm});
            skArc(sketch, "E167.filletArc", {"start": v(-1.03, 9.95) * mm, "mid": v(-1.06, 9.77) * mm, "end": v(-0.9, 9.72) * mm});
            skPoint(sketch, "E168.visualSharp", {"position": v(-0.79, 9) * mm});
            skArc(sketch, "E168.filletArc", {"start": v(1.57, 10.55) * mm, "mid": v(1.6, 9.97) * mm, "end": v(2.17, 9.92) * mm});
            skPoint(sketch, "E169.visualSharp", {"position": v(1.33, 8.48) * mm});
            skArc(sketch, "E169.filletArc", {"start": v(2.37, 8.9) * mm, "mid": v(2.15, 8.47) * mm, "end": v(2.46, 8.1) * mm});
            skPoint(sketch, "E170.visualSharp", {"position": v(-2.1, 15.1) * mm});
            skArc(sketch, "E170.filletArc", {"start": v(-0.93, 15.34) * mm, "mid": v(-1.26, 15) * mm, "end": v(-1.1, 14.56) * mm});
            skPoint(sketch, "E171.visualSharp", {"position": v(0.45, 15.7) * mm});
            skArc(sketch, "E171.filletArc", {"start": v(0.65, 15.48) * mm, "mid": v(0.44, 15.63) * mm, "end": v(0.18, 15.63) * mm});
            skPoint(sketch, "E172.visualSharp", {"position": v(1.69, 16.07) * mm});
            skArc(sketch, "E172.filletArc", {"start": v(2.3, 16.2) * mm, "mid": v(2, 15.95) * mm, "end": v(2.01, 15.56) * mm});
            skPoint(sketch, "E173.visualSharp", {"position": v(7.6, 13.64) * mm});
            skArc(sketch, "E173.filletArc", {"start": v(7.07, 13.5) * mm, "mid": v(7.36, 13.74) * mm, "end": v(7.36, 14.12) * mm});
            skPoint(sketch, "E174.visualSharp", {"position": v(6.07, 17.13) * mm});
            skArc(sketch, "E174.filletArc", {"start": v(6.2, 16.78) * mm, "mid": v(6, 17) * mm, "end": v(5.7, 17.06) * mm});
            skPoint(sketch, "E175.visualSharp", {"position": v(4.48, 16.81) * mm});
            skArc(sketch, "E175.filletArc", {"start": v(5.04, 16.92) * mm, "mid": v(4.74, 16.7) * mm, "end": v(4.72, 16.32) * mm});
            skPoint(sketch, "E176.visualSharp", {"position": v(4.9, 12.93) * mm});
            skArc(sketch, "E176.filletArc", {"start": v(5.06, 13.6) * mm, "mid": v(5.2, 13.21) * mm, "end": v(5.6, 13.11) * mm});
            skPoint(sketch, "E177.visualSharp", {"position": v(4.56, 11.63) * mm});
            skArc(sketch, "E177.filletArc", {"start": v(4.78, 11.7) * mm, "mid": v(4.6, 11.6) * mm, "end": v(4.5, 11.42) * mm});
            skPoint(sketch, "E178.visualSharp", {"position": v(7.97, 12.69) * mm});
            skArc(sketch, "E178.filletArc", {"start": v(8.13, 12.34) * mm, "mid": v(7.9, 12.56) * mm, "end": v(7.6, 12.57) * mm});
            skPoint(sketch, "E179.visualSharp", {"position": v(12.4, 13.94) * mm});
            skArc(sketch, "E179.filletArc", {"start": v(12.46, 13.73) * mm, "mid": v(12.36, 13.9) * mm, "end": v(12.2, 14.02) * mm});
            skPoint(sketch, "E180.visualSharp", {"position": v(6.86, 16.91) * mm});
            skArc(sketch, "E180.filletArc", {"start": v(8.04, 16.13) * mm, "mid": v(7.52, 16.09) * mm, "end": v(7.4, 15.58) * mm});
            skPoint(sketch, "E181.visualSharp", {"position": v(11.06, 7.5) * mm});
            skArc(sketch, "E181.filletArc", {"start": v(10.33, 7.4) * mm, "mid": v(10.68, 7.66) * mm, "end": v(10.63, 8.1) * mm});
            skPoint(sketch, "E182.visualSharp", {"position": v(12.6, 6.86) * mm});
            skArc(sketch, "E182.filletArc", {"start": v(11.93, 6.7) * mm, "mid": v(12.25, 6.98) * mm, "end": v(12.19, 7.4) * mm});
            skPoint(sketch, "E183.visualSharp", {"position": v(19.07, 2.38) * mm});
            skArc(sketch, "E183.filletArc", {"start": v(17.77, 2.6) * mm, "mid": v(18.22, 2.83) * mm, "end": v(18.16, 3.33) * mm});
            skPoint(sketch, "E184.visualSharp", {"position": v(13.81, 13.13) * mm});
            skArc(sketch, "E184.filletArc", {"start": v(14.75, 12.73) * mm, "mid": v(14.27, 12.64) * mm, "end": v(14.17, 12.17) * mm});
            skArc(sketch, "E185.filletArc", {"start": v(27.17, 8.98) * mm, "mid": v(27.04, 9.12) * mm, "end": v(26.86, 9.2) * mm});
            skArc(sketch, "E186.filletArc", {"start": v(31.66, -0.55) * mm, "mid": v(32.15, -0.41) * mm, "end": v(32.2, 0.09) * mm});
            skPoint(sketch, "E187.newPointA", {"position": v(34.82, 0) * mm});
            skArc(sketch, "E187.filletArc", {"start": v(34.6, -0.23) * mm, "mid": v(34.71, 0.02) * mm, "end": v(34.67, 0.29) * mm});
            skArc(sketch, "E188.filletArc", {"start": v(33.62, -0.41) * mm, "mid": v(33.95, -0.64) * mm, "end": v(34.32, -0.5) * mm});
            skArc(sketch, "E189", {"start": v(29.24, 8.78) * mm, "mid": v(29.67, 8.73) * mm, "end": v(30.1, 8.7) * mm});
            skArc(sketch, "E190", {"start": v(50.5, 5.14) * mm, "mid": v(42.82, 4.26) * mm, "end": v(35.86, 0.89) * mm});
            skArc(sketch, "E191", {"start": v(32.14, 8.5) * mm, "mid": v(41.33, 8.43) * mm, "end": v(50.43, 9.78) * mm});
            skLineSegment(sketch, "E192", {"start": v(50.97, 9.35) * mm, "end": v(50.97, 5.58) * mm});
            skPoint(sketch, "E193.visualSharp", {"position": v(31.34, 8.58) * mm});
            skArc(sketch, "E193.filletArc", {"start": v(32.14, 8.5) * mm, "mid": v(31.73, 8.3) * mm, "end": v(31.7, 7.86) * mm});
            skPoint(sketch, "E194.visualSharp", {"position": v(35.45, 0.59) * mm});
            skArc(sketch, "E194.filletArc", {"start": v(35.21, 1.05) * mm, "mid": v(35.5, 0.82) * mm, "end": v(35.86, 0.89) * mm});
            skPoint(sketch, "E195.visualSharp", {"position": v(28.32, 8.96) * mm});
            skArc(sketch, "E195.filletArc", {"start": v(29.24, 8.78) * mm, "mid": v(28.8, 8.6) * mm, "end": v(28.79, 8.12) * mm});
            skPoint(sketch, "E196.visualSharp", {"position": v(30.35, 8.68) * mm});
            skArc(sketch, "E196.filletArc", {"start": v(30.47, 8.46) * mm, "mid": v(30.32, 8.62) * mm, "end": v(30.1, 8.7) * mm});
            skPoint(sketch, "E197.visualSharp", {"position": v(20.26, 2.25) * mm});
            skArc(sketch, "E197.filletArc", {"start": v(20.16, 2.37) * mm, "mid": v(20.28, 2.27) * mm, "end": v(20.42, 2.23) * mm});
            skPoint(sketch, "E198.visualSharp", {"position": v(50.97, 9.9) * mm});
            skArc(sketch, "E198.filletArc", {"start": v(50.97, 9.35) * mm, "mid": v(50.8, 9.7) * mm, "end": v(50.43, 9.78) * mm});
            skPoint(sketch, "E199.visualSharp", {"position": v(50.97, 5.1) * mm});
            skArc(sketch, "E199.filletArc", {"start": v(50.5, 5.14) * mm, "mid": v(50.84, 5.26) * mm, "end": v(50.97, 5.58) * mm});
            skArc(sketch, "E200", {"start": v(-12.1, 0.1) * mm, "mid": v(-12.52, 0.47) * mm, "end": v(-12.96, 0.8) * mm});
            skArc(sketch, "E201", {"start": v(-10.25, 0.9) * mm, "mid": v(-11.42, 1.3) * mm, "end": v(-12.61, 1.6) * mm});
            skArc(sketch, "E202", {"start": v(-11.82, 0) * mm, "mid": v(-11.08, 0) * mm, "end": v(-10.35, 0.05) * mm});
            skPoint(sketch, "E203.visualSharp", {"position": v(-15.13, 1.92) * mm});
            skArc(sketch, "E203.filletArc", {"start": v(-12.61, 1.6) * mm, "mid": v(-13.1, 1.34) * mm, "end": v(-12.96, 0.8) * mm});
            skPoint(sketch, "E204.visualSharp", {"position": v(-11.98, 0) * mm});
            skArc(sketch, "E204.filletArc", {"start": v(-12.1, 0.1) * mm, "mid": v(-11.97, 0.02) * mm, "end": v(-11.82, 0) * mm});
            skPoint(sketch, "E205.visualSharp", {"position": v(-8.92, 0.34) * mm});
            skArc(sketch, "E205.filletArc", {"start": v(-10.35, 0.05) * mm, "mid": v(-9.96, 0.44) * mm, "end": v(-10.25, 0.9) * mm});
            skSolve(sketch);
        }
        {
            var Q0;
            Q0=makeQuery(id+"F4.imprint","IMPRINT",FACE,{"disambiguationData":[TD([[makeQuery(id+"F4.imprint","IMPRINT",EDGE,{"derivedFrom":sQuery(id+"F4.wireOp",EDGE,"E21")}),1.0]])]});
            var Q1;
            Q1=makeQuery(id+"F4.imprint","IMPRINT",FACE,{"disambiguationData":[TD([[makeQuery(id+"F4.imprint","IMPRINT",EDGE,{"derivedFrom":sQuery(id+"F4.wireOp",EDGE,"E94")}),-1.0]])]});
            var Q2;
            Q2=makeQuery(id+"F4.imprint","IMPRINT",FACE,{"disambiguationData":[TD([[makeQuery(id+"F4.imprint","IMPRINT",EDGE,{"derivedFrom":sQuery(id+"F4.wireOp",EDGE,"E91")}),-1.0]])]});
            var Q3;
            Q3=makeQuery(id+"F4.imprint","IMPRINT",FACE,{"disambiguationData":[TD([[makeQuery(id+"F4.imprint","IMPRINT",EDGE,{"derivedFrom":sQuery(id+"F4.wireOp",EDGE,"E77")}),1.0]])]});
            var Q4;
            Q4=makeQuery(id+"F4.imprint","IMPRINT",FACE,{"disambiguationData":[TD([[makeQuery(id+"F4.imprint","IMPRINT",EDGE,{"derivedFrom":sQuery(id+"F4.wireOp",EDGE,"E88")}),-1.0]])]});
            var Q5;
            Q5=makeQuery(id+"F4.imprint","IMPRINT",FACE,{"disambiguationData":[TD([[makeQuery(id+"F4.imprint","IMPRINT",EDGE,{"derivedFrom":sQuery(id+"F4.wireOp",EDGE,"E97")}),-1.0]])]});
            var Q6;
            Q6=makeQuery(id+"F4.imprint","IMPRINT",FACE,{"disambiguationData":[TD([[makeQuery(id+"F4.imprint","IMPRINT",EDGE,{"derivedFrom":sQuery(id+"F4.wireOp",EDGE,"E50")}),1.0]])]});
            var Q7;
            Q7=makeQuery(id+"F4.imprint","IMPRINT",FACE,{"disambiguationData":[TD([[makeQuery(id+"F4.imprint","IMPRINT",EDGE,{"derivedFrom":sQuery(id+"F4.wireOp",EDGE,"E100")}),-1.0]])]});
            var Q8;
            Q8=makeQuery(id+"F4.imprint","IMPRINT",FACE,{"disambiguationData":[TD([[makeQuery(id+"F4.imprint","IMPRINT",EDGE,{"derivedFrom":sQuery(id+"F4.wireOp",EDGE,"E74")}),-1.0]])]});
            var Q9;
            Q9=makeQuery(id+"F4.imprint","IMPRINT",FACE,{"disambiguationData":[TD([[makeQuery(id+"F4.imprint","IMPRINT",EDGE,{"derivedFrom":sQuery(id+"F4.wireOp",EDGE,"E70")}),1.0]])]});
            var Q10;
            Q10=makeQuery(id+"F4.imprint","IMPRINT",FACE,{"disambiguationData":[TD([[makeQuery(id+"F4.imprint","IMPRINT",EDGE,{"derivedFrom":sQuery(id+"F4.wireOp",EDGE,"E44")}),-1.0]])]});
            var Q11;
            Q11=makeQuery(id+"F4.imprint","IMPRINT",FACE,{"disambiguationData":[TD([[makeQuery(id+"F4.imprint","IMPRINT",EDGE,{"derivedFrom":sQuery(id+"F4.wireOp",EDGE,"E29")}),-1.0]])]});
            var Q12;
            Q12=makeQuery(id+"F4.imprint","IMPRINT",FACE,{"disambiguationData":[TD([[makeQuery(id+"F4.imprint","IMPRINT",EDGE,{"derivedFrom":sQuery(id+"F4.wireOp",EDGE,"E103")}),-1.0]])]});
            var Q13;
            Q13=makeQuery(id+"F4.imprint","IMPRINT",FACE,{"disambiguationData":[TD([[makeQuery(id+"F4.imprint","IMPRINT",EDGE,{"derivedFrom":sQuery(id+"F4.wireOp",EDGE,"E200")}),-1.0]])]});
            var Q14;
            Q14=makeQuery(id+"F4.imprint","IMPRINT",FACE,{"disambiguationData":[TD([[makeQuery(id+"F4.imprint","IMPRINT",EDGE,{"derivedFrom":sQuery(id+"F4.wireOp",EDGE,"E64")}),-1.0]])]});
            var Q15;
            Q15=makeQuery(id+"F4.imprint","IMPRINT",FACE,{"disambiguationData":[TD([[makeQuery(id+"F4.imprint","IMPRINT",EDGE,{"derivedFrom":sQuery(id+"F4.wireOp",EDGE,"E67")}),-1.0]])]});
            var Q16;
            Q16=makeQuery(id+"F4.imprint","IMPRINT",FACE,{"disambiguationData":[TD([[makeQuery(id+"F4.imprint","IMPRINT",EDGE,{"derivedFrom":sQuery(id+"F4.wireOp",EDGE,"E61")}),-1.0]])]});
            var Q17;
            Q17=makeQuery(id+"F4.imprint","IMPRINT",FACE,{"disambiguationData":[TD([[makeQuery(id+"F4.imprint","IMPRINT",EDGE,{"derivedFrom":sQuery(id+"F4.wireOp",EDGE,"E55")}),-1.0]])]});
            var Q18;
            Q18=makeQuery(id+"F4.imprint","IMPRINT",FACE,{"disambiguationData":[TD([[makeQuery(id+"F4.imprint","IMPRINT",EDGE,{"derivedFrom":sQuery(id+"F4.wireOp",EDGE,"E58")}),-1.0]])]});
            var Q19;
            Q19=makeQuery(id+"F4.imprint","IMPRINT",FACE,{"disambiguationData":[TD([[makeQuery(id+"F4.imprint","IMPRINT",EDGE,{"derivedFrom":sQuery(id+"F4.wireOp",EDGE,"E109")}),-1.0]])]});
            var Q20;
            Q20=makeQuery(id+"F4.imprint","IMPRINT",FACE,{"disambiguationData":[TD([[makeQuery(id+"F4.imprint","IMPRINT",EDGE,{"derivedFrom":sQuery(id+"F4.wireOp",EDGE,"E106")}),-1.0]])]});
            var Q21;
            Q21=makeQuery(id+"F4.imprint","IMPRINT",FACE,{"disambiguationData":[TD([[makeQuery(id+"F4.imprint","IMPRINT",EDGE,{"derivedFrom":sQuery(id+"F4.wireOp",EDGE,"E25")}),-1.0]])]});
            var Q22;
            Q22=makeQuery(id+"F4.imprint","IMPRINT",FACE,{"disambiguationData":[TD([[makeQuery(id+"F4.imprint","IMPRINT",EDGE,{"derivedFrom":sQuery(id+"F4.wireOp",EDGE,"E117")}),1.0]])]});
            var Q23;
            Q23=makeQuery(id+"F4.imprint","IMPRINT",FACE,{"disambiguationData":[TD([[makeQuery(id+"F4.imprint","IMPRINT",EDGE,{"derivedFrom":sQuery(id+"F4.wireOp",EDGE,"E28")}),-1.0]])]});
            extrude(context, id + "F5", {"entities" : qUnion([Q0, Q1, Q2, Q3, Q4, Q5, Q6, Q7, Q8, Q9, Q10, Q11, Q12, Q13, Q14, Q15, Q16, Q17, Q18, Q19, Q20, Q21, Q22, Q23]), "operationType" : NewBodyOperationType.REMOVE, "oppositeDirection" : true, "depth" : 0.76 * mm});
        }
        {
            var Q0;
            {var subQ0=sQuery(id+"F0.wireOp",EDGE,"E7");Q0=makeQuery(id+"F0.imprint","IMPRINT",FACE,{"disambiguationData":[TD([[makeQuery(id+"F0.imprint","IMPRINT",EDGE,{"derivedFrom":subQ0}),-1.0]])]});}
            extrude(context, id + "F6", {"entities" : qUnion([Q0]), "operationType" : NewBodyOperationType.ADD, "depth" : 2.54 * mm});
        }
    });
